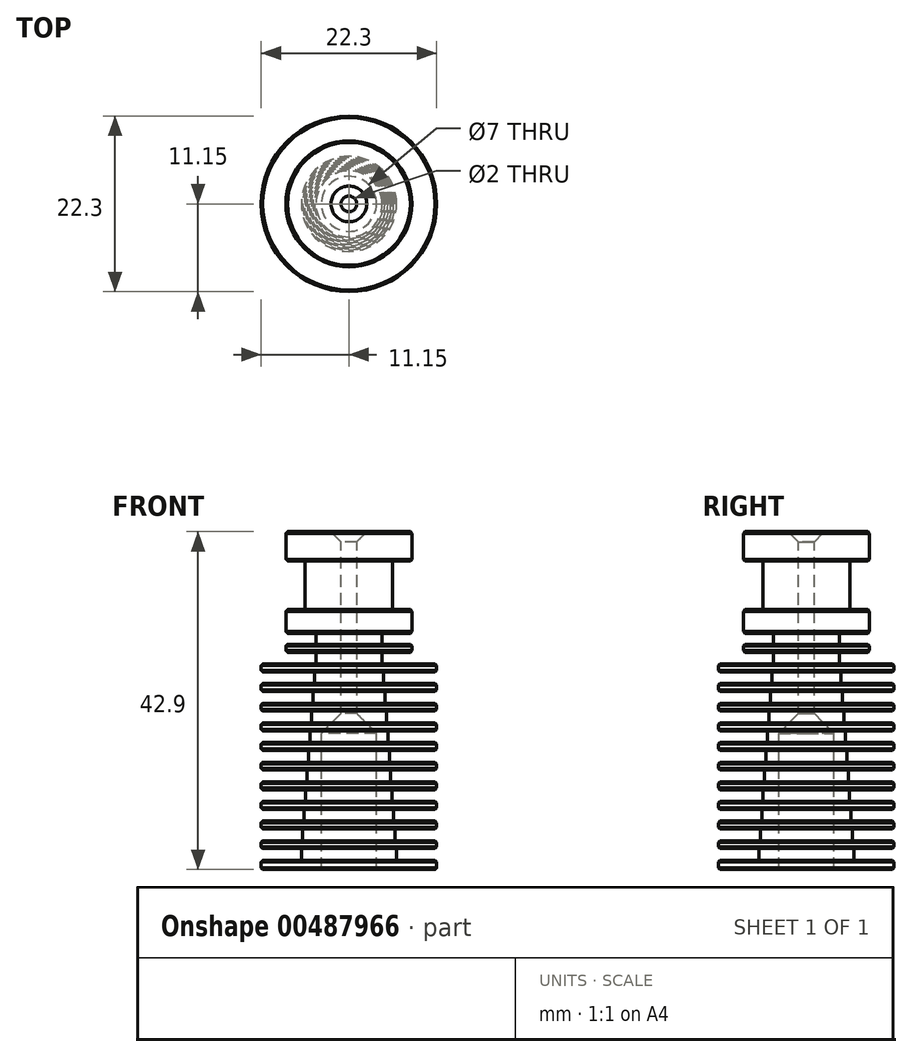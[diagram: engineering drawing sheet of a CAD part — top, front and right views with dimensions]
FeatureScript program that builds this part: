
annotation { "Feature Type Name" : "Feature", "Feature Type Description" : "" }
export const myFeature = defineFeature(function(context is Context, id is Id, definition is map)
    precondition{}
    {
        {
            var Q0;
            Q0=qCreatedBy(makeId("Front.planeOp"),FACE);
            var sketch = newSketch(context, id + "F0", { "sketchPlane" : qUnion([Q0])});
            skLineSegment(sketch, "E0.bottom", {"start": v(11.15, 0) * mm, "end": v(-11.15, 0) * mm});
            skLineSegment(sketch, "E1", {"start": v(0, 42.9) * mm, "end": v(0, 0) * mm, "construction": true});
            skLineSegment(sketch, "E2", {"start": v(-11.15, 0) * mm, "end": v(-11.15, 1.15) * mm});
            skLineSegment(sketch, "E3", {"start": v(-11.15, 1.15) * mm, "end": v(-6.05, 1.15) * mm});
            skLineSegment(sketch, "E4", {"start": v(11.15, 1.15) * mm, "end": v(11.15, 0) * mm});
            skLineSegment(sketch, "E5.bottom", {"start": v(-11.15, 2.65) * mm, "end": v(-6.05, 2.65) * mm});
            skLineSegment(sketch, "E5.top", {"start": v(-11.15, 3.65) * mm, "end": v(-5.87, 3.65) * mm});
            skLineSegment(sketch, "E5.left", {"start": v(-11.15, 2.65) * mm, "end": v(-11.15, 3.65) * mm});
            skLineSegment(sketch, "E5.right", {"start": v(11.15, 2.65) * mm, "end": v(11.15, 3.65) * mm});
            skLineSegment(sketch, "E6", {"start": v(-6.05, 2.65) * mm, "end": v(-6.05, 1.15) * mm});
            skLineSegment(sketch, "E7", {"start": v(6.05, 2.65) * mm, "end": v(6.05, 1.15) * mm});
            skLineSegment(sketch, "E8.bottom", {"start": v(-11.15, 5.14) * mm, "end": v(-5.87, 5.14) * mm});
            skLineSegment(sketch, "E8.top", {"start": v(-11.15, 6.14) * mm, "end": v(-5.68, 6.14) * mm});
            skLineSegment(sketch, "E8.left", {"start": v(-11.15, 5.14) * mm, "end": v(-11.15, 6.14) * mm});
            skLineSegment(sketch, "E8.right", {"start": v(11.15, 5.14) * mm, "end": v(11.15, 6.14) * mm});
            skLineSegment(sketch, "E9.bottom", {"start": v(-11.15, 7.63) * mm, "end": v(-5.68, 7.63) * mm});
            skLineSegment(sketch, "E9.top", {"start": v(-11.15, 8.63) * mm, "end": v(-5.5, 8.63) * mm});
            skLineSegment(sketch, "E9.left", {"start": v(-11.15, 7.63) * mm, "end": v(-11.15, 8.64) * mm});
            skLineSegment(sketch, "E9.right", {"start": v(11.15, 7.63) * mm, "end": v(11.15, 8.64) * mm});
            skLineSegment(sketch, "E10.bottom", {"start": v(-11.15, 10.13) * mm, "end": v(-5.5, 10.13) * mm});
            skLineSegment(sketch, "E10.top", {"start": v(-11.15, 11.13) * mm, "end": v(-5.31, 11.13) * mm});
            skLineSegment(sketch, "E10.left", {"start": v(-11.15, 10.13) * mm, "end": v(-11.15, 11.13) * mm});
            skLineSegment(sketch, "E10.right", {"start": v(11.15, 10.13) * mm, "end": v(11.15, 11.13) * mm});
            skLineSegment(sketch, "E11.bottom", {"start": v(-11.15, 12.62) * mm, "end": v(-5.31, 12.62) * mm});
            skLineSegment(sketch, "E11.top", {"start": v(-11.15, 13.62) * mm, "end": v(-5.13, 13.62) * mm});
            skLineSegment(sketch, "E11.left", {"start": v(-11.15, 12.63) * mm, "end": v(-11.15, 13.62) * mm});
            skLineSegment(sketch, "E11.right", {"start": v(11.15, 12.63) * mm, "end": v(11.15, 13.62) * mm});
            skLineSegment(sketch, "E12.bottom", {"start": v(-11.15, 15.12) * mm, "end": v(-5.13, 15.12) * mm});
            skLineSegment(sketch, "E12.top", {"start": v(-11.15, 16.12) * mm, "end": v(-4.94, 16.12) * mm});
            skLineSegment(sketch, "E12.left", {"start": v(-11.15, 15.12) * mm, "end": v(-11.15, 16.12) * mm});
            skLineSegment(sketch, "E12.right", {"start": v(11.15, 15.12) * mm, "end": v(11.15, 16.12) * mm});
            skLineSegment(sketch, "E13.bottom", {"start": v(-11.15, 17.62) * mm, "end": v(-4.94, 17.62) * mm});
            skLineSegment(sketch, "E13.top", {"start": v(-11.15, 18.61) * mm, "end": v(-4.75, 18.61) * mm});
            skLineSegment(sketch, "E13.left", {"start": v(-11.15, 17.62) * mm, "end": v(-11.15, 18.62) * mm});
            skLineSegment(sketch, "E13.right", {"start": v(11.15, 17.62) * mm, "end": v(11.15, 18.62) * mm});
            skLineSegment(sketch, "E14.bottom", {"start": v(-11.15, 20.1) * mm, "end": v(-4.76, 20.1) * mm});
            skLineSegment(sketch, "E14.top", {"start": v(-11.15, 21.1) * mm, "end": v(-4.57, 21.1) * mm});
            skLineSegment(sketch, "E14.left", {"start": v(-11.15, 20.11) * mm, "end": v(-11.15, 21.1) * mm});
            skLineSegment(sketch, "E14.right", {"start": v(11.15, 20.11) * mm, "end": v(11.15, 21.1) * mm});
            skLineSegment(sketch, "E15.bottom", {"start": v(-11.15, 22.6) * mm, "end": v(-4.57, 22.6) * mm});
            skLineSegment(sketch, "E15.top", {"start": v(-11.15, 23.6) * mm, "end": v(-4.39, 23.6) * mm});
            skLineSegment(sketch, "E15.left", {"start": v(-11.15, 22.6) * mm, "end": v(-11.15, 23.6) * mm});
            skLineSegment(sketch, "E15.right", {"start": v(11.15, 22.6) * mm, "end": v(11.15, 23.6) * mm});
            skLineSegment(sketch, "E16.bottom", {"start": v(-11.15, 25.1) * mm, "end": v(-4.38, 25.1) * mm});
            skLineSegment(sketch, "E16.top", {"start": v(-11.15, 26.1) * mm, "end": v(-4.2, 26.1) * mm});
            skLineSegment(sketch, "E16.left", {"start": v(-11.15, 25.1) * mm, "end": v(-11.15, 26.1) * mm});
            skLineSegment(sketch, "E16.right", {"start": v(11.15, 25.1) * mm, "end": v(11.15, 26.1) * mm});
            skLineSegment(sketch, "E17", {"start": v(-5.87, 3.65) * mm, "end": v(-5.87, 5.14) * mm});
            skLineSegment(sketch, "E18", {"start": v(-5.68, 6.14) * mm, "end": v(-5.68, 7.64) * mm});
            skLineSegment(sketch, "E19", {"start": v(-5.5, 8.63) * mm, "end": v(-5.5, 10.13) * mm});
            skLineSegment(sketch, "E20", {"start": v(-5.31, 11.13) * mm, "end": v(-5.31, 12.63) * mm});
            skLineSegment(sketch, "E21", {"start": v(-5.12, 13.62) * mm, "end": v(-5.12, 15.12) * mm});
            skLineSegment(sketch, "E22", {"start": v(-4.94, 16.12) * mm, "end": v(-4.94, 17.62) * mm});
            skLineSegment(sketch, "E23", {"start": v(-4.75, 18.62) * mm, "end": v(-4.75, 20.11) * mm});
            skLineSegment(sketch, "E24", {"start": v(5.87, 3.65) * mm, "end": v(5.87, 5.14) * mm});
            skLineSegment(sketch, "E25", {"start": v(5.68, 6.14) * mm, "end": v(5.68, 7.64) * mm});
            skLineSegment(sketch, "E26", {"start": v(5.5, 8.64) * mm, "end": v(5.5, 10.13) * mm});
            skLineSegment(sketch, "E27", {"start": v(5.31, 11.13) * mm, "end": v(5.31, 12.62) * mm});
            skLineSegment(sketch, "E28", {"start": v(5.12, 13.63) * mm, "end": v(5.12, 15.12) * mm});
            skLineSegment(sketch, "E29", {"start": v(4.94, 16.12) * mm, "end": v(4.94, 17.62) * mm});
            skLineSegment(sketch, "E30", {"start": v(4.75, 18.62) * mm, "end": v(4.75, 20.11) * mm});
            skLineSegment(sketch, "E31", {"start": v(-4.57, 21.1) * mm, "end": v(-4.57, 22.6) * mm});
            skLineSegment(sketch, "E32", {"start": v(-4.38, 23.6) * mm, "end": v(-4.38, 25.1) * mm});
            skLineSegment(sketch, "E33", {"start": v(-4.2, 26.1) * mm, "end": v(-4.2, 27.6) * mm});
            skLineSegment(sketch, "E34", {"start": v(4.57, 21.1) * mm, "end": v(4.57, 22.6) * mm});
            skLineSegment(sketch, "E35", {"start": v(4.38, 23.6) * mm, "end": v(4.38, 25.1) * mm});
            skLineSegment(sketch, "E36", {"start": v(4.2, 26.1) * mm, "end": v(4.2, 27.6) * mm});
            skLineSegment(sketch, "E37", {"start": v(-6.05, 2.64) * mm, "end": v(-4.2, 27.6) * mm, "construction": true});
            skLineSegment(sketch, "E38.bottom", {"start": v(-8, 27.6) * mm, "end": v(-4.2, 27.6) * mm});
            skLineSegment(sketch, "E38.top", {"start": v(-8, 28.6) * mm, "end": v(-4.2, 28.6) * mm});
            skLineSegment(sketch, "E38.left", {"start": v(-8, 27.6) * mm, "end": v(-8, 28.6) * mm});
            skLineSegment(sketch, "E38.right", {"start": v(8, 27.6) * mm, "end": v(8, 28.6) * mm});
            skLineSegment(sketch, "E39.bottom", {"start": v(-8, 33) * mm, "end": v(-5.55, 33) * mm});
            skLineSegment(sketch, "E39.top", {"start": v(-8, 30) * mm, "end": v(-4.2, 30) * mm});
            skLineSegment(sketch, "E39.left", {"start": v(-8, 33) * mm, "end": v(-8, 30) * mm});
            skLineSegment(sketch, "E39.right", {"start": v(8, 33) * mm, "end": v(8, 30) * mm});
            skLineSegment(sketch, "E40", {"start": v(-4.2, 28.6) * mm, "end": v(-4.2, 30) * mm});
            skLineSegment(sketch, "E41", {"start": v(4.2, 28.6) * mm, "end": v(4.2, 30) * mm});
            skLineSegment(sketch, "E42.bottom", {"start": v(-8, 39.2) * mm, "end": v(-5.55, 39.2) * mm});
            skLineSegment(sketch, "E42.top", {"start": v(-8, 42.9) * mm, "end": v(-2.27, 42.9) * mm});
            skLineSegment(sketch, "E42.left", {"start": v(-8, 39.2) * mm, "end": v(-8, 42.9) * mm});
            skLineSegment(sketch, "E42.right", {"start": v(8, 39.2) * mm, "end": v(8, 42.9) * mm});
            skLineSegment(sketch, "E43.trimOffspring", {"start": v(5.55, 39.2) * mm, "end": v(8, 39.2) * mm});
            skLineSegment(sketch, "E44.trimOffspring", {"start": v(5.55, 33) * mm, "end": v(8, 33) * mm});
            skLineSegment(sketch, "E45.trimOffspring", {"start": v(4.2, 30) * mm, "end": v(8, 30) * mm});
            skLineSegment(sketch, "E46.trimOffspring", {"start": v(4.2, 28.6) * mm, "end": v(8, 28.6) * mm});
            skLineSegment(sketch, "E47.trimOffspring", {"start": v(4.2, 27.6) * mm, "end": v(8, 27.6) * mm});
            skLineSegment(sketch, "E48.trimOffspring", {"start": v(4.2, 26.1) * mm, "end": v(11.15, 26.1) * mm});
            skLineSegment(sketch, "E49.trimOffspring", {"start": v(4.38, 25.1) * mm, "end": v(11.15, 25.1) * mm});
            skLineSegment(sketch, "E50.trimOffspring", {"start": v(4.39, 23.6) * mm, "end": v(11.15, 23.6) * mm});
            skLineSegment(sketch, "E51.trimOffspring", {"start": v(4.57, 22.6) * mm, "end": v(11.15, 22.6) * mm});
            skLineSegment(sketch, "E52.trimOffspring", {"start": v(4.57, 21.1) * mm, "end": v(11.15, 21.1) * mm});
            skLineSegment(sketch, "E53.trimOffspring", {"start": v(4.75, 20.1) * mm, "end": v(11.15, 20.1) * mm});
            skLineSegment(sketch, "E54.trimOffspring", {"start": v(4.75, 18.61) * mm, "end": v(11.15, 18.61) * mm});
            skLineSegment(sketch, "E55.trimOffspring", {"start": v(4.94, 17.62) * mm, "end": v(11.15, 17.62) * mm});
            skLineSegment(sketch, "E56.trimOffspring", {"start": v(4.94, 16.12) * mm, "end": v(11.15, 16.12) * mm});
            skLineSegment(sketch, "E57.trimOffspring", {"start": v(5.12, 15.12) * mm, "end": v(11.15, 15.12) * mm});
            skLineSegment(sketch, "E58.trimOffspring", {"start": v(5.13, 13.62) * mm, "end": v(11.15, 13.62) * mm});
            skLineSegment(sketch, "E59.trimOffspring", {"start": v(5.31, 12.62) * mm, "end": v(11.15, 12.62) * mm});
            skLineSegment(sketch, "E60.trimOffspring", {"start": v(5.31, 11.13) * mm, "end": v(11.15, 11.13) * mm});
            skLineSegment(sketch, "E61.trimOffspring", {"start": v(5.5, 10.13) * mm, "end": v(11.15, 10.13) * mm});
            skLineSegment(sketch, "E62.trimOffspring", {"start": v(5.5, 8.63) * mm, "end": v(11.15, 8.63) * mm});
            skLineSegment(sketch, "E63.trimOffspring", {"start": v(5.68, 7.63) * mm, "end": v(11.15, 7.63) * mm});
            skLineSegment(sketch, "E64.trimOffspring", {"start": v(5.68, 6.14) * mm, "end": v(11.15, 6.14) * mm});
            skLineSegment(sketch, "E65.trimOffspring", {"start": v(5.87, 5.14) * mm, "end": v(11.15, 5.14) * mm});
            skLineSegment(sketch, "E66.trimOffspring", {"start": v(6.05, 2.65) * mm, "end": v(11.15, 2.65) * mm});
            skLineSegment(sketch, "E67.trimOffspring", {"start": v(6.05, 1.15) * mm, "end": v(11.15, 1.15) * mm});
            skLineSegment(sketch, "E68.trimOffspring", {"start": v(5.87, 3.65) * mm, "end": v(11.15, 3.65) * mm});
            skLineSegment(sketch, "E69", {"start": v(-2.27, 42.9) * mm, "end": v(-1, 41.63) * mm});
            skLineSegment(sketch, "E70", {"start": v(-1, 41.63) * mm, "end": v(-1, 19.8) * mm});
            skLineSegment(sketch, "E71", {"start": v(2.27, 42.9) * mm, "end": v(1, 41.63) * mm});
            skLineSegment(sketch, "E72", {"start": v(1, 41.63) * mm, "end": v(1, 19.8) * mm});
            skLineSegment(sketch, "E73.trimOffspring", {"start": v(2.27, 42.9) * mm, "end": v(8, 42.9) * mm});
            skLineSegment(sketch, "E74", {"start": v(-2.27, 42.9) * mm, "end": v(2.27, 42.9) * mm, "construction": true});
            skLineSegment(sketch, "E75", {"start": v(-4.2, 30) * mm, "end": v(4.2, 30) * mm, "construction": true});
            skLineSegment(sketch, "E76", {"start": v(-4.2, 28.6) * mm, "end": v(4.2, 28.6) * mm, "construction": true});
            skLineSegment(sketch, "E77", {"start": v(-4.2, 27.6) * mm, "end": v(4.2, 27.6) * mm, "construction": true});
            skLineSegment(sketch, "E78", {"start": v(-4.2, 26.1) * mm, "end": v(4.2, 26.1) * mm, "construction": true});
            skLineSegment(sketch, "E79", {"start": v(-4.38, 25.1) * mm, "end": v(4.38, 25.1) * mm, "construction": true});
            skLineSegment(sketch, "E80", {"start": v(-4.39, 23.6) * mm, "end": v(4.39, 23.6) * mm, "construction": true});
            skLineSegment(sketch, "E81", {"start": v(-4.57, 22.6) * mm, "end": v(4.57, 22.6) * mm, "construction": true});
            skLineSegment(sketch, "E82", {"start": v(-4.57, 21.1) * mm, "end": v(4.57, 21.1) * mm, "construction": true});
            skLineSegment(sketch, "E83", {"start": v(-4.76, 20.1) * mm, "end": v(4.75, 20.1) * mm, "construction": true});
            skLineSegment(sketch, "E84", {"start": v(-4.75, 18.61) * mm, "end": v(4.75, 18.61) * mm, "construction": true});
            skLineSegment(sketch, "E85", {"start": v(-4.94, 17.62) * mm, "end": v(4.94, 17.62) * mm, "construction": true});
            skLineSegment(sketch, "E86", {"start": v(-4.94, 16.12) * mm, "end": v(4.94, 16.12) * mm, "construction": true});
            skLineSegment(sketch, "E87", {"start": v(-5.13, 15.12) * mm, "end": v(5.12, 15.12) * mm, "construction": true});
            skLineSegment(sketch, "E88", {"start": v(-5.13, 13.62) * mm, "end": v(5.13, 13.62) * mm, "construction": true});
            skLineSegment(sketch, "E89", {"start": v(-5.31, 12.62) * mm, "end": v(5.31, 12.62) * mm, "construction": true});
            skLineSegment(sketch, "E90", {"start": v(-5.31, 11.13) * mm, "end": v(5.31, 11.13) * mm, "construction": true});
            skLineSegment(sketch, "E91", {"start": v(-5.5, 10.13) * mm, "end": v(5.5, 10.13) * mm, "construction": true});
            skLineSegment(sketch, "E92", {"start": v(-5.5, 8.63) * mm, "end": v(5.5, 8.63) * mm, "construction": true});
            skLineSegment(sketch, "E93", {"start": v(-5.68, 7.63) * mm, "end": v(5.68, 7.63) * mm, "construction": true});
            skLineSegment(sketch, "E94", {"start": v(-5.68, 6.14) * mm, "end": v(5.68, 6.14) * mm, "construction": true});
            skLineSegment(sketch, "E95", {"start": v(-5.87, 5.14) * mm, "end": v(5.87, 5.14) * mm, "construction": true});
            skLineSegment(sketch, "E96", {"start": v(-5.87, 3.65) * mm, "end": v(5.87, 3.65) * mm, "construction": true});
            skLineSegment(sketch, "E97", {"start": v(-6.05, 2.65) * mm, "end": v(6.05, 2.65) * mm, "construction": true});
            skLineSegment(sketch, "E98", {"start": v(-6.05, 1.15) * mm, "end": v(6.05, 1.15) * mm, "construction": true});
            skLineSegment(sketch, "E99.left", {"start": v(-3.5, 0) * mm, "end": v(-3.5, 17.3) * mm});
            skLineSegment(sketch, "E99.right", {"start": v(3.5, 0) * mm, "end": v(3.5, 17.3) * mm});
            skLineSegment(sketch, "E100", {"start": v(3.5, 17.3) * mm, "end": v(1, 19.8) * mm});
            skLineSegment(sketch, "E101", {"start": v(-3.5, 17.3) * mm, "end": v(-1, 19.8) * mm});
            skLineSegment(sketch, "E102", {"start": v(-5.55, 33) * mm, "end": v(-5.55, 39.2) * mm});
            skLineSegment(sketch, "E103", {"start": v(5.55, 33) * mm, "end": v(5.55, 39.2) * mm});
            skLineSegment(sketch, "E104", {"start": v(-5.55, 33) * mm, "end": v(5.55, 33) * mm, "construction": true});
            skLineSegment(sketch, "E105", {"start": v(-5.55, 39.2) * mm, "end": v(5.55, 39.2) * mm, "construction": true});
            skSolve(sketch);
        }
        {
            var Q0;
            {var subQ0=sQuery(id+"F0.wireOp",EDGE,"E2");Q0=makeQuery(id+"F0.imprint","IMPRINT",FACE,{"disambiguationData":[TD([[makeQuery(id+"F0.imprint","IMPRINT",EDGE,{"derivedFrom":subQ0}),-1.0]])]});}
            var Q1;
            Q1=sQuery(id+"F0.wireOp",EDGE,"E1");
            revolve(context, id + "F1", {"surfaceOperationType" : NewSurfaceOperationType.NEW, "entities" : qUnion([Q0]), "axis" : qUnion([Q1]), "revolveType" : RevolveType.FULL});
        }
        {
            var Q0;
            Q0=makeQuery(id+"F1.opRevolve","SWEPT_FACE",FACE,{"disambiguationData":[OSD([sQuery(id+"F0.wireOp",EDGE,"E42.left")])]});
            var Q1;
            Q1=makeQuery(id+"F1.opRevolve","SWEPT_FACE",FACE,{"disambiguationData":[OSD([sQuery(id+"F0.wireOp",EDGE,"E39.left")])]});
            var Q2;
            Q2=makeQuery(id+"F1.opRevolve","SWEPT_FACE",FACE,{"disambiguationData":[OSD([sQuery(id+"F0.wireOp",EDGE,"E38.left")])]});
            var Q3;
            Q3=makeQuery(id+"F1.opRevolve","SWEPT_FACE",FACE,{"disambiguationData":[OSD([sQuery(id+"F0.wireOp",EDGE,"E16.left")])]});
            var Q4;
            Q4=makeQuery(id+"F1.opRevolve","SWEPT_FACE",FACE,{"disambiguationData":[OSD([sQuery(id+"F0.wireOp",EDGE,"E15.left")])]});
            var Q5;
            Q5=makeQuery(id+"F1.opRevolve","SWEPT_FACE",FACE,{"disambiguationData":[OSD([sQuery(id+"F0.wireOp",EDGE,"E14.left")])]});
            var Q6;
            Q6=makeQuery(id+"F1.opRevolve","SWEPT_FACE",FACE,{"disambiguationData":[OSD([sQuery(id+"F0.wireOp",EDGE,"E13.left")])]});
            var Q7;
            Q7=makeQuery(id+"F1.opRevolve","SWEPT_FACE",FACE,{"disambiguationData":[OSD([sQuery(id+"F0.wireOp",EDGE,"E12.left")])]});
            var Q8;
            Q8=makeQuery(id+"F1.opRevolve","SWEPT_FACE",FACE,{"disambiguationData":[OSD([sQuery(id+"F0.wireOp",EDGE,"E11.left")])]});
            var Q9;
            Q9=makeQuery(id+"F1.opRevolve","SWEPT_FACE",FACE,{"disambiguationData":[OSD([sQuery(id+"F0.wireOp",EDGE,"E10.left")])]});
            var Q10;
            Q10=makeQuery(id+"F1.opRevolve","SWEPT_FACE",FACE,{"disambiguationData":[OSD([sQuery(id+"F0.wireOp",EDGE,"E9.left")])]});
            var Q11;
            Q11=makeQuery(id+"F1.opRevolve","SWEPT_FACE",FACE,{"disambiguationData":[OSD([sQuery(id+"F0.wireOp",EDGE,"E8.left")])]});
            var Q12;
            Q12=makeQuery(id+"F1.opRevolve","SWEPT_FACE",FACE,{"disambiguationData":[OSD([sQuery(id+"F0.wireOp",EDGE,"E5.left")])]});
            var Q13;
            Q13=makeQuery(id+"F1.opRevolve","SWEPT_FACE",FACE,{"disambiguationData":[OSD([sQuery(id+"F0.wireOp",EDGE,"E2")])]});
            chamfer(context, id + "F2", {"entities" : qUnion([Q0, Q1, Q2, Q3, Q4, Q5, Q6, Q7, Q8, Q9, Q10, Q11, Q12, Q13]), "width" : 0.2 * mm, "tangentPropagation" : true});
        }
    });
